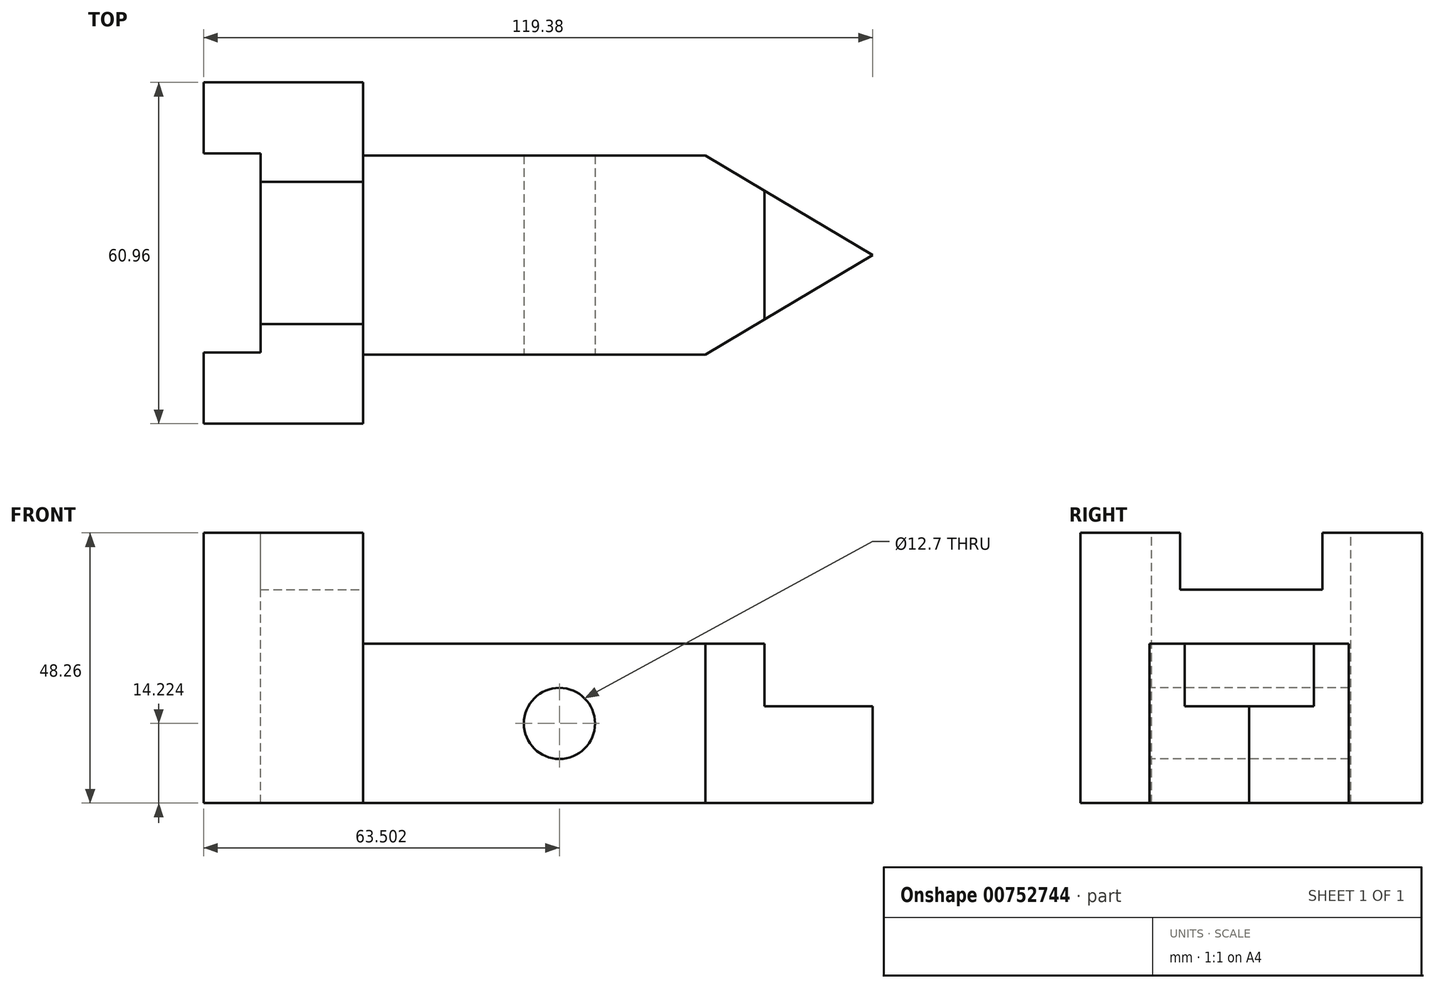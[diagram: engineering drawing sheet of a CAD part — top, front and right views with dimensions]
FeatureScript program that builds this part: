
annotation { "Feature Type Name" : "Feature", "Feature Type Description" : "" }
export const myFeature = defineFeature(function(context is Context, id is Id, definition is map)
    precondition{}
    {
        {
            var Q0;
            Q0=qCreatedBy(makeId("Top.planeOp"),FACE);
            var sketch = newSketch(context, id + "F0", { "sketchPlane" : qUnion([Q0])});
            skLineSegment(sketch, "E0.bottom", {"start": v(-28.45, -30.12) * mm, "end": v(0, -30.12) * mm});
            skLineSegment(sketch, "E0.top", {"start": v(-28.45, 30.84) * mm, "end": v(0, 30.84) * mm});
            skLineSegment(sketch, "E0.left", {"start": v(-28.45, -30.12) * mm, "end": v(-28.45, 30.84) * mm});
            skLineSegment(sketch, "E0.right", {"start": v(0, -30.12) * mm, "end": v(0, 30.84) * mm});
            skLineSegment(sketch, "E1.bottom", {"start": v(0, -17.78) * mm, "end": v(61.1, -17.78) * mm});
            skLineSegment(sketch, "E1.top", {"start": v(0, 17.78) * mm, "end": v(61.1, 17.78) * mm});
            skLineSegment(sketch, "E1.left", {"start": v(0, -17.78) * mm, "end": v(0, 17.78) * mm});
            skLineSegment(sketch, "E1.right", {"start": v(61.1, -17.78) * mm, "end": v(61.1, 17.78) * mm});
            skLineSegment(sketch, "E2", {"start": v(61.1, -17.78) * mm, "end": v(90.93, 0) * mm});
            skLineSegment(sketch, "E3", {"start": v(90.93, 0) * mm, "end": v(61.1, 17.78) * mm});
            skSolve(sketch);
        }
        {
            var Q0;
            {var subQ1=sQuery(id+"F0.wireOp",EDGE,"E0.bottom");Q0=makeQuery(id+"F0.imprint","IMPRINT",FACE,{"disambiguationData":[TD([[makeQuery(id+"F0.imprint","IMPRINT",EDGE,{"derivedFrom":subQ1}),1.0]])]});}
            extrude(context, id + "F1", {"entities" : qUnion([Q0]), "depth" : 48.26 * mm, "offsetDistance" : 25.4 * mm});
        }
        {
            var Q0;
            Q0=makeQuery(id+"F0.imprint","IMPRINT",FACE,{"disambiguationData":[TD([[makeQuery(id+"F0.imprint","IMPRINT",EDGE,{"derivedFrom":sQuery(id+"F0.wireOp",EDGE,"E1.bottom")}),1.0]])]});
            extrude(context, id + "F2", {"entities" : qUnion([Q0]), "operationType" : NewBodyOperationType.ADD, "depth" : 28.45 * mm, "offsetDistance" : 25.4 * mm});
        }
        {
            var Q0;
            Q0=makeQuery(id+"F0.imprint","IMPRINT",FACE,{"disambiguationData":[TD([[makeQuery(id+"F0.imprint","IMPRINT",EDGE,{"derivedFrom":sQuery(id+"F0.wireOp",EDGE,"E1.right")}),-1.0]])]});
            extrude(context, id + "F3", {"entities" : qUnion([Q0]), "operationType" : NewBodyOperationType.ADD, "depth" : 28.45 * mm, "offsetDistance" : 25.4 * mm});
        }
        {
            var Q0;
            Q0=makeQuery(id+"F1.opExtrude","CAP_FACE",FACE,{"disambiguationData":[OSD([sQuery(id+"F0.wireOp",EDGE,"E0.bottom"),sQuery(id+"F0.wireOp",EDGE,"E0.top"),sQuery(id+"F0.wireOp",EDGE,"E0.left"),sQuery(id+"F0.wireOp",EDGE,"E0.right"),sQuery(id+"F0.wireOp",EDGE,"E1.left")])],"isStart":false});
            var sketch = newSketch(context, id + "F4", { "sketchPlane" : qUnion([Q0])});
            skLineSegment(sketch, "E4.bottom", {"start": v(-28.45, -17.42) * mm, "end": v(-18.29, -17.42) * mm});
            skLineSegment(sketch, "E4.top", {"start": v(-28.45, 18.14) * mm, "end": v(-18.29, 18.14) * mm});
            skLineSegment(sketch, "E4.left", {"start": v(-28.45, -17.42) * mm, "end": v(-28.45, 18.14) * mm});
            skLineSegment(sketch, "E4.right", {"start": v(-18.29, -17.42) * mm, "end": v(-18.29, 18.14) * mm});
            skLineSegment(sketch, "E5.bottom", {"start": v(-18.29, -12.34) * mm, "end": v(0, -12.34) * mm});
            skLineSegment(sketch, "E5.top", {"start": v(-18.29, 13.06) * mm, "end": v(0, 13.06) * mm});
            skLineSegment(sketch, "E5.left", {"start": v(-18.29, -12.34) * mm, "end": v(-18.29, 13.06) * mm});
            skLineSegment(sketch, "E5.right", {"start": v(0, -12.34) * mm, "end": v(0, 13.06) * mm});
            skSolve(sketch);
        }
        {
            var Q0;
            {var subQ1=sQuery(id+"F4.wireOp",EDGE,"E4.bottom");Q0=makeQuery(id+"F4.imprint","IMPRINT",FACE,{"disambiguationData":[TD([[makeQuery(id+"F4.imprint","IMPRINT",EDGE,{"derivedFrom":subQ1}),1.0]])]});}
            extrude(context, id + "F5", {"entities" : qUnion([Q0]), "operationType" : NewBodyOperationType.REMOVE, "oppositeDirection" : true, "depth" : 48.26 * mm, "offsetDistance" : 25.4 * mm});
        }
        {
            var Q0;
            Q0=makeQuery(id+"F4.imprint","IMPRINT",FACE,{"disambiguationData":[TD([[makeQuery(id+"F4.imprint","IMPRINT",EDGE,{"derivedFrom":sQuery(id+"F4.wireOp",EDGE,"E5.bottom")}),1.0]])]});
            extrude(context, id + "F6", {"entities" : qUnion([Q0]), "operationType" : NewBodyOperationType.REMOVE, "oppositeDirection" : true, "depth" : 10.16 * mm, "offsetDistance" : 25.4 * mm});
        }
        {
            var Q0;
            {var subQ0=sQuery(id+"F0.wireOp",EDGE,"E1.right");Q0=makeQuery(id+"F3.boolean.opBoolean","MERGE",FACE,{"derivedFrom":[makeQuery(id+"F2.opExtrude","CAP_FACE",FACE,{"disambiguationData":[OSD([sQuery(id+"F0.wireOp",EDGE,"E1.bottom"),sQuery(id+"F0.wireOp",EDGE,"E1.top"),sQuery(id+"F0.wireOp",EDGE,"E1.left"),subQ0])],"isStart":false}),makeQuery(id+"F3.opExtrude","CAP_FACE",FACE,{"disambiguationData":[OSD([subQ0,sQuery(id+"F0.wireOp",EDGE,"E2"),sQuery(id+"F0.wireOp",EDGE,"E3")])],"isStart":false})]});}
            var sketch = newSketch(context, id + "F7", { "sketchPlane" : qUnion([Q0])});
            skLineSegment(sketch, "E6", {"start": v(71.63, 11.5) * mm, "end": v(71.63, -11.5) * mm});
            skSolve(sketch);
        }
        {
            var Q0;
            {var subQ0=sQuery(id+"F7.wireOp",EDGE,"E6");Q0=makeQuery(id+"F7.imprint","IMPRINT",FACE,{"disambiguationData":[TD([[makeQuery(id+"F7.imprint","IMPRINT",EDGE,{"derivedFrom":subQ0}),1.0]])]});}
            extrude(context, id + "F8", {"entities" : qUnion([Q0]), "operationType" : NewBodyOperationType.REMOVE, "oppositeDirection" : true, "depth" : 11.18 * mm, "offsetDistance" : 25.4 * mm});
        }
        {
            var Q0;
            Q0=makeQuery(id+"F2.opExtrude","SWEPT_FACE",FACE,{"disambiguationData":[OSD([sQuery(id+"F0.wireOp",EDGE,"E1.bottom")])]});
            var sketch = newSketch(context, id + "F9", { "sketchPlane" : qUnion([Q0])});
            skCircle(sketch, "E7", {"center": v(35.05, 14.22) * mm, "radius": 6.35 * mm});
            skSolve(sketch);
        }
        {
            var Q0;
            Q0=makeQuery(id+"F9.imprint","IMPRINT",FACE,{"disambiguationData":[TD([[makeQuery(id+"F9.imprint","IMPRINT",EDGE,{"derivedFrom":sQuery(id+"F9.wireOp",EDGE,"E7")}),1.0]])]});
            extrude(context, id + "F10", {"entities" : qUnion([Q0]), "operationType" : NewBodyOperationType.REMOVE, "oppositeDirection" : true, "depth" : 35.56 * mm, "offsetDistance" : 25.4 * mm});
        }
    });
